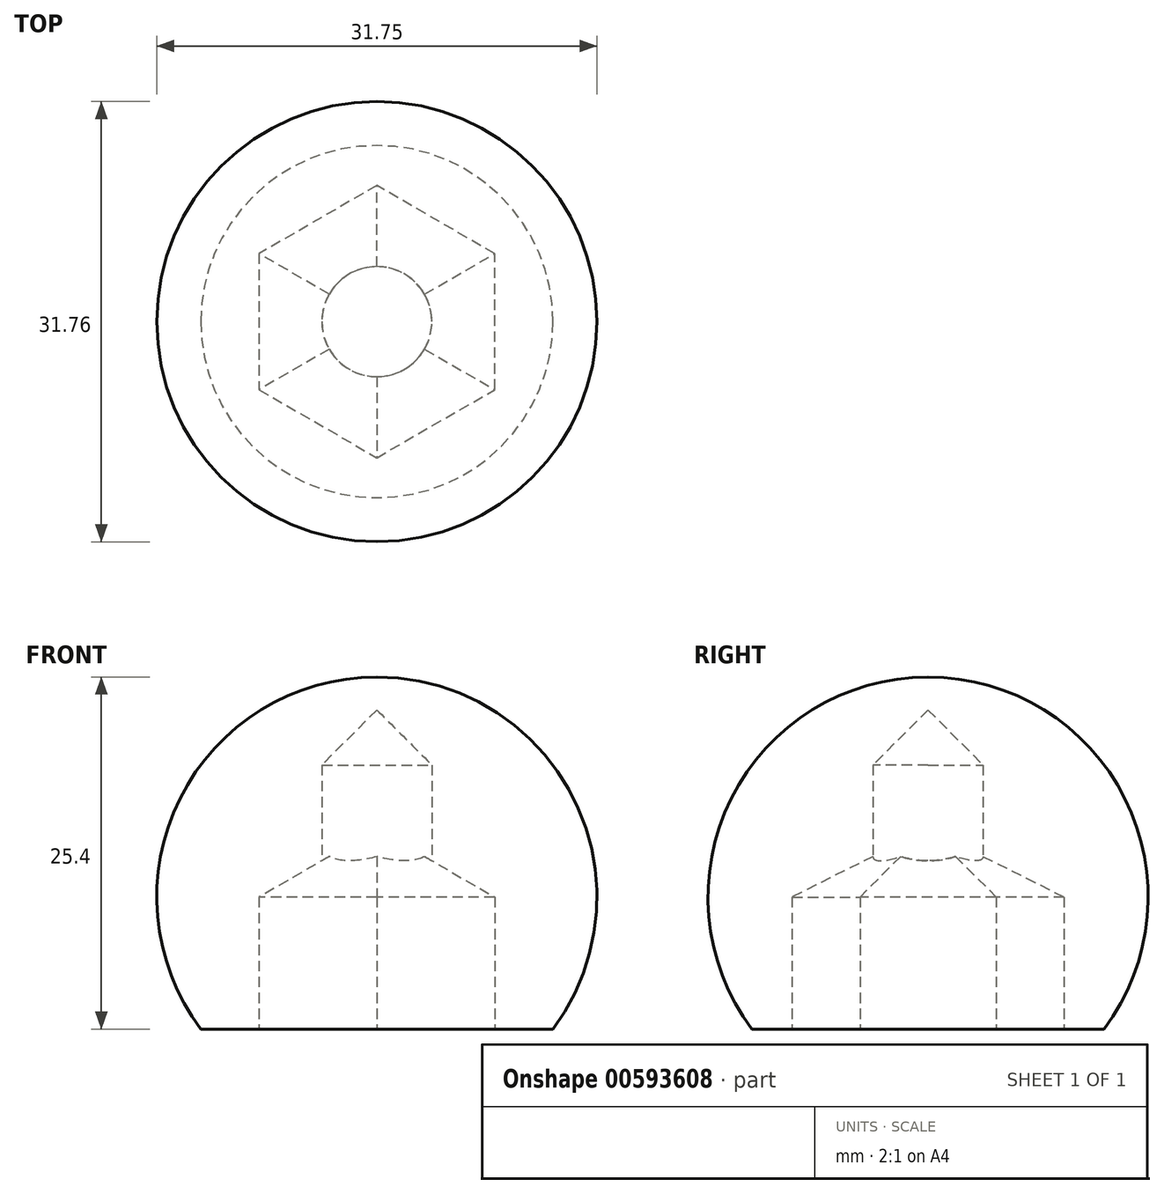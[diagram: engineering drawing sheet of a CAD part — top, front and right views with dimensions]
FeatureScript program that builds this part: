
annotation { "Feature Type Name" : "Feature", "Feature Type Description" : "" }
export const myFeature = defineFeature(function(context is Context, id is Id, definition is map)
    precondition{}
    {
        {
            var Q0;
            Q0=qCreatedBy(makeId("Front.planeOp"),FACE);
            var sketch = newSketch(context, id + "F0", { "sketchPlane" : qUnion([Q0])});
            skArc(sketch, "E0", {"start": v(12.7, 0) * mm, "mid": v(14.2, 16.62) * mm, "end": v(0, 25.4) * mm});
            skPoint(sketch, "E1", {"position": v(12.7, 0) * mm});
            skLineSegment(sketch, "E2", {"start": v(0, 0) * mm, "end": v(12.7, 0) * mm});
            skLineSegment(sketch, "E3", {"start": v(0, 0) * mm, "end": v(0, 25.4) * mm});
            skSolve(sketch);
        }
        {
            var Q0;
            Q0=makeQuery(id+"F0.imprint","IMPRINT",FACE,{"disambiguationData":[TD([[makeQuery(id+"F0.imprint","IMPRINT",EDGE,{"derivedFrom":sQuery(id+"F0.wireOp",EDGE,"E0")}),1.0]])]});
            var Q1;
            Q1=sQuery(id+"F0.wireOp",EDGE,"E3");
            revolve(context, id + "F1", {"entities" : qUnion([Q0]), "axis" : qUnion([Q1]), "revolveType" : RevolveType.FULL});
        }
        {
            var Q0;
            Q0=makeQuery(id+"F1.opRevolve","SWEPT_FACE",FACE,{"disambiguationData":[OSD([sQuery(id+"F0.wireOp",EDGE,"E2")])]});
            var sketch = newSketch(context, id + "F2", { "sketchPlane" : qUnion([Q0])});
            skCircle(sketch, "E4", {"center": v(0, 0) * mm, "radius": 3.97 * mm});
            skSolve(sketch);
        }
        {
            var Q0;
            Q0=makeQuery(id+"F2.imprint","IMPRINT",FACE,{"disambiguationData":[TD([[makeQuery(id+"F2.imprint","IMPRINT",EDGE,{"derivedFrom":sQuery(id+"F2.wireOp",EDGE,"E4")}),1.0]])]});
            extrude(context, id + "F3", {"entities" : qUnion([Q0]), "operationType" : NewBodyOperationType.REMOVE, "oppositeDirection" : true, "depth" : 19.05 * mm, "offsetDistance" : 25.4 * mm});
        }
        {
            var Q0;
            Q0=makeQuery(id+"F3.boolean.opBoolean","COPY",FACE,{"derivedFrom":makeQuery(id+"F3.opExtrude","CAP_FACE",FACE,{"disambiguationData":[OSD([sQuery(id+"F2.wireOp",EDGE,"E4")])],"isStart":false})});
            extrude(context, id + "F4", {"entities" : qUnion([Q0]), "operationType" : NewBodyOperationType.REMOVE, "oppositeDirection" : true, "depth" : 25.4 * mm, "offsetDistance" : 25.4 * mm, "hasDraft" : true, "draftAngle" : 45 * degree, "draftPullDirection" : true});
        }
        {
            var Q0;
            Q0=makeQuery(id+"F1.opRevolve","SWEPT_FACE",FACE,{"disambiguationData":[OSD([sQuery(id+"F0.wireOp",EDGE,"E2")])]});
            var sketch = newSketch(context, id + "F5", { "sketchPlane" : qUnion([Q0])});
            skCircle(sketch, "E5.cCircle", {"center": v(0, 0) * mm, "radius": 8.5 * mm, "construction": true});
            skLineSegment(sketch, "E5.0", {"start": v(-8.5, -4.9) * mm, "end": v(-8.5, 4.9) * mm});
            skLineSegment(sketch, "E5.1", {"start": v(-8.5, 4.9) * mm, "end": v(0, 9.81) * mm});
            skLineSegment(sketch, "E5.2", {"start": v(0, 9.81) * mm, "end": v(8.5, 4.9) * mm});
            skLineSegment(sketch, "E5.3", {"start": v(8.5, 4.9) * mm, "end": v(8.5, -4.9) * mm});
            skLineSegment(sketch, "E5.4", {"start": v(8.5, -4.9) * mm, "end": v(0, -9.81) * mm});
            skLineSegment(sketch, "E5.5", {"start": v(0, -9.81) * mm, "end": v(-8.5, -4.9) * mm});
            skPoint(sketch, "E5.0.midPoint", {"position": v(-8.5, 0) * mm});
            skSolve(sketch);
        }
        {
            var Q0;
            Q0=makeQuery(id+"F5.imprint","IMPRINT",FACE,{"disambiguationData":[TD([[makeQuery(id+"F5.imprint","IMPRINT",EDGE,{"derivedFrom":sQuery(id+"F5.wireOp",EDGE,"E5.0")}),-1.0]])]});
            extrude(context, id + "F6", {"entities" : qUnion([Q0]), "operationType" : NewBodyOperationType.REMOVE, "oppositeDirection" : true, "depth" : 9.52 * mm, "offsetDistance" : 25.4 * mm});
        }
        {
            var Q0;
            Q0=makeQuery(id+"F6.boolean.opBoolean","COPY",FACE,{"derivedFrom":makeQuery(id+"F6.opExtrude","CAP_FACE",FACE,{"disambiguationData":[OSD([sQuery(id+"F2.wireOp",EDGE,"E4"),sQuery(id+"F5.wireOp",EDGE,"E5.0"),sQuery(id+"F5.wireOp",EDGE,"E5.1"),sQuery(id+"F5.wireOp",EDGE,"E5.2"),sQuery(id+"F5.wireOp",EDGE,"E5.3"),sQuery(id+"F5.wireOp",EDGE,"E5.4"),sQuery(id+"F5.wireOp",EDGE,"E5.5")])],"isStart":false})});
            var sketch = newSketch(context, id + "F7", { "sketchPlane" : qUnion([Q0])});
            skCircle(sketch, "E6", {"center": v(0, 0) * mm, "radius": 3.97 * mm});
            skSolve(sketch);
        }
        {
            var Q0;
            Q0 = qSketchRegion(id + "F7", true);
            var Q1;
            Q1=makeQuery(id+"F7.imprint","IMPRINT",FACE,{"disambiguationData":[TD([[makeQuery(id+"F7.imprint","IMPRINT",EDGE,{"derivedFrom":sQuery(id+"F7.wireOp",EDGE,"E6")}),-1.0]])]});
            extrude(context, id + "F8", {"entities" : qUnion([Q0, Q1]), "operationType" : NewBodyOperationType.REMOVE, "oppositeDirection" : true, "depth" : 3.17 * mm, "offsetDistance" : 25.4 * mm, "hasDraft" : true, "draftAngle" : 60 * degree, "draftPullDirection" : true});
        }
    });
